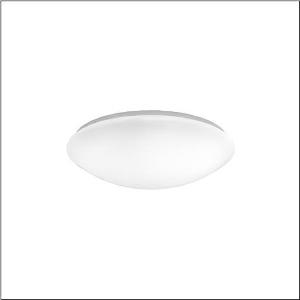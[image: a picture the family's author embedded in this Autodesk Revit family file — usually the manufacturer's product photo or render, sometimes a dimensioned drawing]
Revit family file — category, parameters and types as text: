
# Revit family: round_31_b_5pja112001a
name_source: partatom
category: Lighting Fixtures
units: mm (PartAtom-declared; Revit-internal decimal feet)

## family parameters
Cut with Voids When Loaded = No
Host = Face
Light Source = No
Part Type = Normal
Room Calculation Point = No
Round Connector Dimension = Use Diameter
Shared = No

## types (1)
- Round 31 B (1 x LED, 2300 lm, 19 W, 3000K)
    Apparent Load = 19 VA
    CIE Flux Codes = 42 71 89 88 100
    Color Rendering = 80
    Color Temperature = 3000K
    Default Elevation = 1800 mm
    Description = Round 31 B, wall and ceiling luminaire, primary optical cover: enclosure, of PMMA, light emission: direct distribution, primary light characteristic: symmetric, installation type: surface-mounted, LED, rated luminous flux: 2.300lm, luminous efficacy: 121lm/W, light colour: 830, colour temperature: 3000K, with terminal, 3+2-pole, max. 2.5mm², mains connection: 230V, AC, 50/60Hz, rated input power: 19W, luminaire housing, round, of steel, white, diameter: 360mm, height: 95mm, protection rating (complete): IP40, insulation class (complete): insulation class I (protective earthing), certification: CE, impact resistance: IK02, permissible operating ambient temperature: -20..+25°C, packaging unit: 1 piece
    Height = 95 mm
    Lamp = 1 x LED
    Lamp Light Flux = 2300 lm
    Lamp Power = 19 W
    Lamp count = 1
    Length = 360 mm
    Luminous efficacy = 121 lm/W
    Manufacturer = Siteco
    ModVariant = No
    Model = 5PJA112001A
    Mounting Place = Ceiling
    Mounting Type = Surface mounted
    Number of Poles = 1
    OnlyDefault = Yes
    Power Factor = 1
    Product Name = Round 31 B
    Product group = wall and ceiling luminaire
    ProductGroupID = 301
    Protection Class = Protection class I
    Protection Degree = IP 40
    RLX_Detail_Level = 1
    RLX_Emergency_Light_Flux = 0 lm
    RLX_Emergency_Type = 0
    RLX_Emergency_Type_DB = No
    RlxData = <blob elided: 10985 chars, md5=05d79baf>
    Socket = socket
    Standby Power = 0 W
    System Light Flux = 2300 lm
    System Power = 19 W
    Type Comments = Product without accessories
    Type Image = l_1258315.jpg
    URL = http://relux.com
    VarID = ---
    Voltage = 0 V
    Weight = 0.00 kg
    Width = 0 mm  [stored 0 ft]

note: [stored X ft] marks values corroborated as IEEE doubles in the binary element streams (Revit-internal decimal feet)

## geometry (parser evidence)
native form markers: Sweep x11
no freeform markers — native parametric forms only
